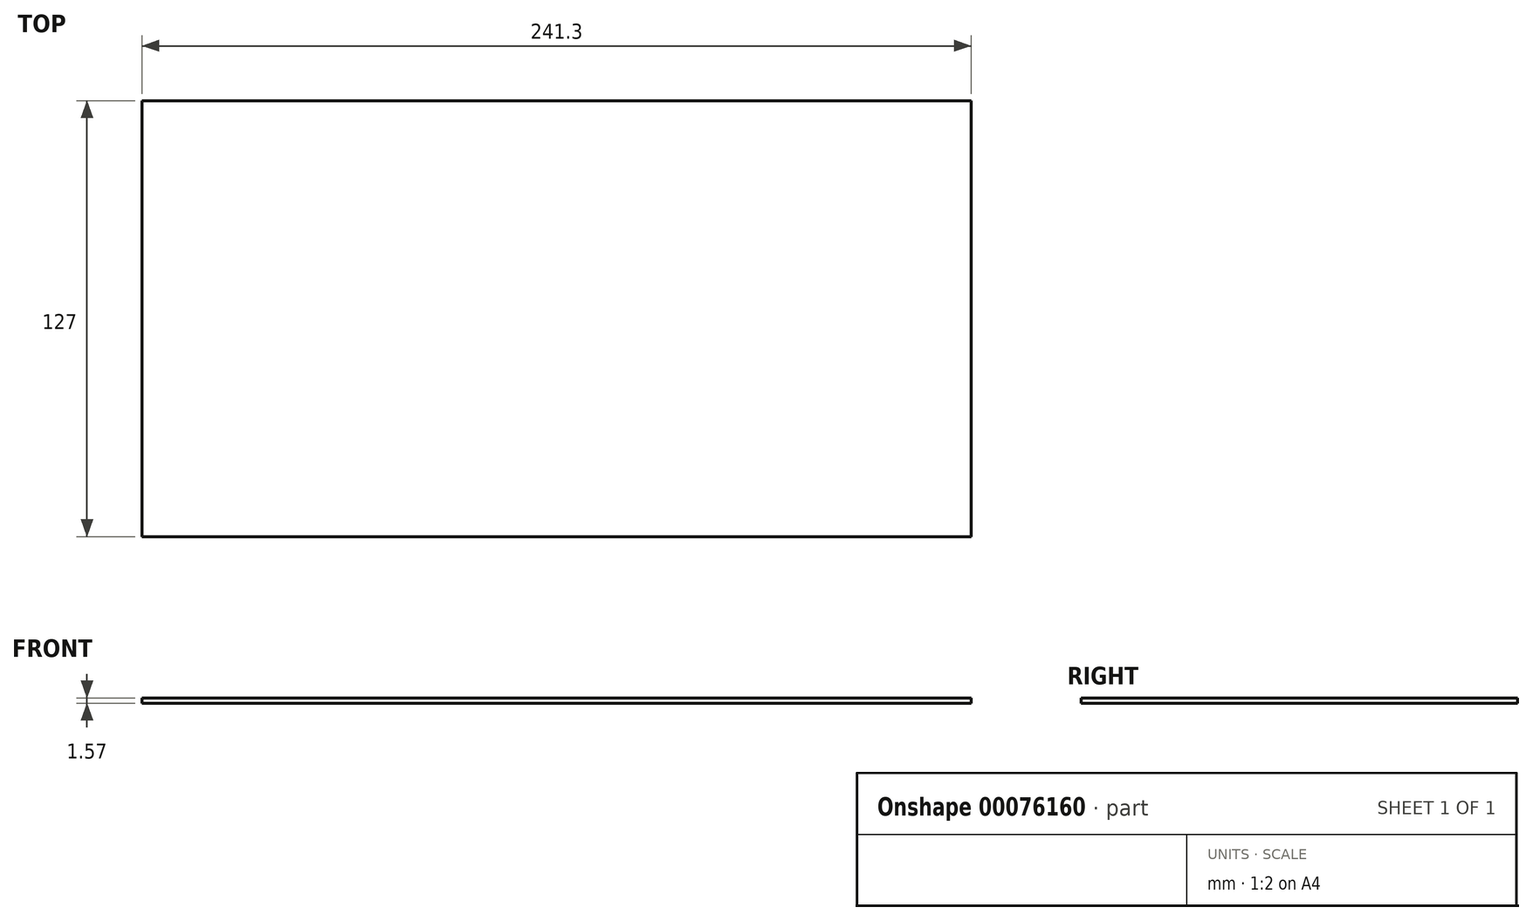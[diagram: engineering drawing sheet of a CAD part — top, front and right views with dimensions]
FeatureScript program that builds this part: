
annotation { "Feature Type Name" : "Feature", "Feature Type Description" : "" }
export const myFeature = defineFeature(function(context is Context, id is Id, definition is map)
    precondition{}
    {
        {
            var Q0;
            Q0=qCreatedBy(makeId("Top.planeOp"),FACE);
            var sketch = newSketch(context, id + "F0", { "sketchPlane" : qUnion([Q0])});
            skLineSegment(sketch, "E0.bottom", {"start": v(120.65, 63.5) * mm, "end": v(-120.65, 63.5) * mm});
            skLineSegment(sketch, "E0.top", {"start": v(120.65, -63.5) * mm, "end": v(-120.65, -63.5) * mm});
            skLineSegment(sketch, "E0.left", {"start": v(120.65, 63.5) * mm, "end": v(120.65, -63.5) * mm});
            skLineSegment(sketch, "E0.right", {"start": v(-120.65, 63.5) * mm, "end": v(-120.65, -63.5) * mm});
            skPoint(sketch, "E0.middle", {"position": v(0, 0) * mm});
            skSolve(sketch);
        }
        {
            var Q0;
            Q0 = qSketchRegion(id + "F0", true);
            extrude(context, id + "F1", {"entities" : qUnion([Q0]), "depth" : 1.57 * mm, "offsetDistance" : 25.4 * mm});
        }
    });
